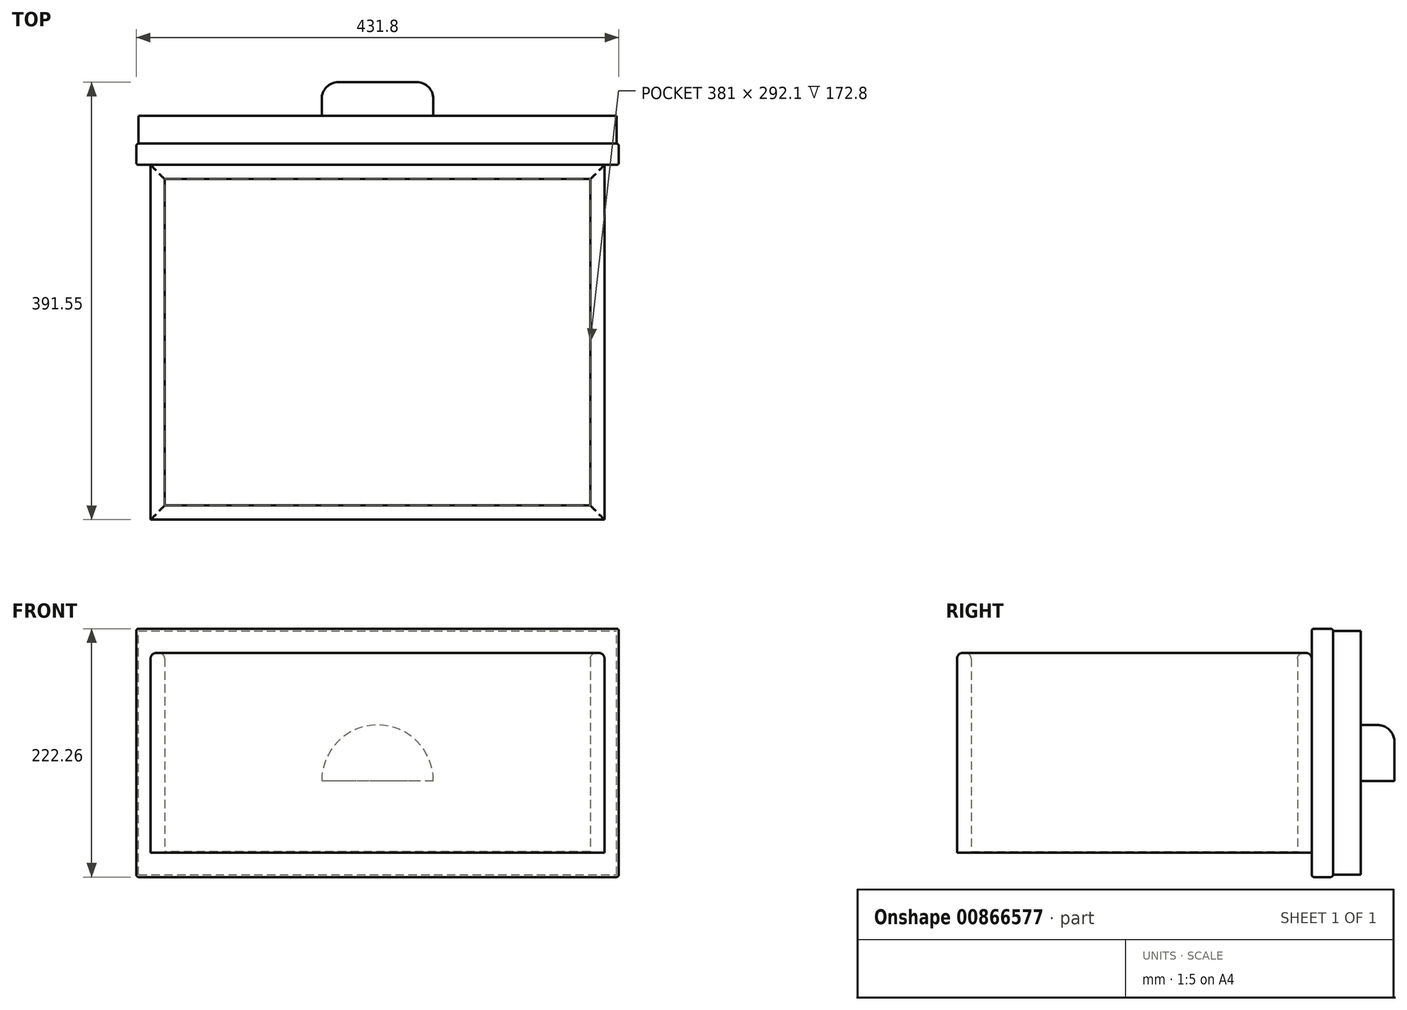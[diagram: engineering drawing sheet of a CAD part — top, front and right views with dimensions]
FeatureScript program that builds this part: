
annotation { "Feature Type Name" : "Feature", "Feature Type Description" : "" }
export const myFeature = defineFeature(function(context is Context, id is Id, definition is map)
    precondition{}
    {
        {
            var Q0;
            Q0=qCreatedBy(makeId("Top.planeOp"),FACE);
            var sketch = newSketch(context, id + "F0", { "sketchPlane" : qUnion([Q0])});
            skLineSegment(sketch, "E0.bottom", {"start": v(203.2, -158.75) * mm, "end": v(-203.2, -158.75) * mm});
            skLineSegment(sketch, "E0.top", {"start": v(203.2, 158.75) * mm, "end": v(-203.2, 158.75) * mm});
            skLineSegment(sketch, "E0.left", {"start": v(203.2, -158.75) * mm, "end": v(203.2, 158.75) * mm});
            skLineSegment(sketch, "E0.right", {"start": v(-203.2, -158.75) * mm, "end": v(-203.2, 158.75) * mm});
            skPoint(sketch, "E0.middle", {"position": v(0, 0) * mm});
            skLineSegment(sketch, "E1.0", {"start": v(190.5, 146.05) * mm, "end": v(-190.5, 146.05) * mm});
            skLineSegment(sketch, "E1.1", {"start": v(190.5, -146.05) * mm, "end": v(190.5, 146.05) * mm});
            skLineSegment(sketch, "E1.2", {"start": v(190.5, -146.05) * mm, "end": v(-190.5, -146.05) * mm});
            skLineSegment(sketch, "E1.3", {"start": v(-190.5, -146.05) * mm, "end": v(-190.5, 146.05) * mm});
            skSolve(sketch);
        }
        {
            var Q0;
            Q0=makeQuery(id+"F0.imprint","IMPRINT",FACE,{"disambiguationData":[TD([[makeQuery(id+"F0.imprint","IMPRINT",EDGE,{"derivedFrom":sQuery(id+"F0.wireOp",EDGE,"E0.bottom")}),-1.0]])]});
            extrude(context, id + "F1", {"entities" : qUnion([Q0]), "depth" : 177.8 * mm, "offsetDistance" : 25 * mm});
        }
        {
            var Q0;
            Q0=makeQuery(id+"F1.opExtrude","CAP_FACE",FACE,{"disambiguationData":[OSD([sQuery(id+"F0.wireOp",EDGE,"E0.bottom"),sQuery(id+"F0.wireOp",EDGE,"E0.top"),sQuery(id+"F0.wireOp",EDGE,"E0.left"),sQuery(id+"F0.wireOp",EDGE,"E0.right"),sQuery(id+"F0.wireOp",EDGE,"E1.0"),sQuery(id+"F0.wireOp",EDGE,"E1.1"),sQuery(id+"F0.wireOp",EDGE,"E1.2"),sQuery(id+"F0.wireOp",EDGE,"E1.3")])],"isStart":true});
            var sketch = newSketch(context, id + "F2", { "sketchPlane" : qUnion([Q0])});
            skLineSegment(sketch, "E2.bottom", {"start": v(203.2, -158.75) * mm, "end": v(-203.2, -158.75) * mm});
            skLineSegment(sketch, "E2.top", {"start": v(203.2, 158.75) * mm, "end": v(-203.2, 158.75) * mm});
            skLineSegment(sketch, "E2.left", {"start": v(203.2, -158.75) * mm, "end": v(203.2, 158.75) * mm});
            skLineSegment(sketch, "E2.right", {"start": v(-203.2, -158.75) * mm, "end": v(-203.2, 158.75) * mm});
            skPoint(sketch, "E2.middle", {"position": v(0, 0) * mm});
            skSolve(sketch);
        }
        {
            var Q0;
            Q0 = qSketchRegion(id + "F2", true);
            extrude(context, id + "F3", {"entities" : qUnion([Q0]), "operationType" : NewBodyOperationType.ADD, "depth" : 1 * mm, "offsetDistance" : 25 * mm});
        }
        {
            var Q0;
            Q0=makeQuery(id+"F3.boolean.opBoolean","MERGE",FACE,{"derivedFrom":[makeQuery(id+"F1.opExtrude","SWEPT_FACE",FACE,{"disambiguationData":[OSD([sQuery(id+"F0.wireOp",EDGE,"E0.top")])]}),makeQuery(id+"F3.opExtrude","SWEPT_FACE",FACE,{"disambiguationData":[OSD([sQuery(id+"F2.wireOp",EDGE,"E2.bottom")])]})]});
            var sketch = newSketch(context, id + "F4", { "sketchPlane" : qUnion([Q0])});
            skLineSegment(sketch, "E3", {"start": v(0, 0) * mm, "end": v(0, 177.8) * mm, "construction": true});
            skLineSegment(sketch, "E4", {"start": v(-203.2, 88.4) * mm, "end": v(203.2, 88.4) * mm, "construction": true});
            skLineSegment(sketch, "E5.bottom", {"start": v(215.9, -22.73) * mm, "end": v(-215.9, -22.73) * mm});
            skLineSegment(sketch, "E5.top", {"start": v(215.9, 199.53) * mm, "end": v(-215.9, 199.52) * mm});
            skLineSegment(sketch, "E5.left", {"start": v(215.9, -22.73) * mm, "end": v(215.9, 199.53) * mm});
            skLineSegment(sketch, "E5.right", {"start": v(-215.9, -22.73) * mm, "end": v(-215.9, 199.52) * mm});
            skPoint(sketch, "E5.middle", {"position": v(0, 88.4) * mm});
            skSolve(sketch);
        }
        {
            var Q0;
            Q0 = qSketchRegion(id + "F4", true);
            extrude(context, id + "F5", {"entities" : qUnion([Q0]), "depth" : 19.05 * mm, "offsetDistance" : 25 * mm});
        }
        {
            var Q0;
            Q0=makeQuery(id+"F1.opExtrude","CAP_EDGE",EDGE,{"disambiguationData":[OSD([sQuery(id+"F0.wireOp",EDGE,"E0.left")])],"isStart":false});
            var Q1;
            Q1=makeQuery(id+"F1.opExtrude","CAP_EDGE",EDGE,{"disambiguationData":[OSD([sQuery(id+"F0.wireOp",EDGE,"E1.1")])],"isStart":false});
            var Q2;
            Q2=makeQuery(id+"F1.opExtrude","CAP_EDGE",EDGE,{"disambiguationData":[OSD([sQuery(id+"F0.wireOp",EDGE,"E1.2")])],"isStart":false});
            var Q3;
            Q3=makeQuery(id+"F1.opExtrude","CAP_EDGE",EDGE,{"disambiguationData":[OSD([sQuery(id+"F0.wireOp",EDGE,"E0.bottom")])],"isStart":false});
            var Q4;
            Q4=makeQuery(id+"F1.opExtrude","CAP_EDGE",EDGE,{"disambiguationData":[OSD([sQuery(id+"F0.wireOp",EDGE,"E1.3")])],"isStart":false});
            var Q5;
            Q5=makeQuery(id+"F1.opExtrude","CAP_EDGE",EDGE,{"disambiguationData":[OSD([sQuery(id+"F0.wireOp",EDGE,"E0.right")])],"isStart":false});
            var Q6;
            Q6=makeQuery(id+"F1.opExtrude","CAP_FACE",FACE,{"disambiguationData":[OSD([sQuery(id+"F0.wireOp",EDGE,"E0.bottom"),sQuery(id+"F0.wireOp",EDGE,"E0.top"),sQuery(id+"F0.wireOp",EDGE,"E0.left"),sQuery(id+"F0.wireOp",EDGE,"E0.right"),sQuery(id+"F0.wireOp",EDGE,"E1.0"),sQuery(id+"F0.wireOp",EDGE,"E1.1"),sQuery(id+"F0.wireOp",EDGE,"E1.2"),sQuery(id+"F0.wireOp",EDGE,"E1.3")])],"isStart":false});
            fillet(context, id + "F6", {"entities" : qUnion([Q0, Q1, Q2, Q3, Q4, Q5, Q6]), "radius" : 5 * mm, "tangentPropagation" : true, "allowEdgeOverflow" : false});
        }
        {
            var Q0;
            Q0=makeQuery(id+"F5.opExtrude","CAP_FACE",FACE,{"disambiguationData":[OSD([sQuery(id+"F4.wireOp",EDGE,"E5.bottom"),sQuery(id+"F4.wireOp",EDGE,"E5.top"),sQuery(id+"F4.wireOp",EDGE,"E5.left"),sQuery(id+"F4.wireOp",EDGE,"E5.right")])],"isStart":false});
            var Q1;
            Q1=makeQuery(id+"F5.opExtrude","SWEPT_FACE",FACE,{"disambiguationData":[OSD([sQuery(id+"F4.wireOp",EDGE,"E5.top")])]});
            var Q2;
            Q2=makeQuery(id+"F5.opExtrude","SWEPT_FACE",FACE,{"disambiguationData":[OSD([sQuery(id+"F4.wireOp",EDGE,"E5.left")])]});
            var Q3;
            Q3=makeQuery(id+"F5.opExtrude","SWEPT_FACE",FACE,{"disambiguationData":[OSD([sQuery(id+"F4.wireOp",EDGE,"E5.bottom")])]});
            var Q4;
            Q4=makeQuery(id+"F5.opExtrude","SWEPT_FACE",FACE,{"disambiguationData":[OSD([sQuery(id+"F4.wireOp",EDGE,"E5.right")])]});
            fillet(context, id + "F7", {"entities" : qUnion([Q0, Q1, Q2, Q3, Q4]), "radius" : 2 * mm, "tangentPropagation" : true, "allowEdgeOverflow" : false});
        }
        {
            var Q0;
            Q0=makeQuery(id+"F5.opExtrude","CAP_FACE",FACE,{"disambiguationData":[OSD([sQuery(id+"F4.wireOp",EDGE,"E5.bottom"),sQuery(id+"F4.wireOp",EDGE,"E5.top"),sQuery(id+"F4.wireOp",EDGE,"E5.left"),sQuery(id+"F4.wireOp",EDGE,"E5.right")])],"isStart":false});
            extrude(context, id + "F8", {"entities" : qUnion([Q0]), "operationType" : NewBodyOperationType.ADD, "depth" : 25 * mm, "offsetDistance" : 25 * mm});
        }
        {
            var Q0;
            Q0=makeQuery(id+"F8.opExtrude","CAP_FACE",FACE,{"disambiguationData":[OSD([sQuery(id+"F4.wireOp",EDGE,"E5.bottom"),sQuery(id+"F4.wireOp",EDGE,"E5.top"),sQuery(id+"F4.wireOp",EDGE,"E5.left"),sQuery(id+"F4.wireOp",EDGE,"E5.right")])],"isStart":false});
            var sketch = newSketch(context, id + "F9", { "sketchPlane" : qUnion([Q0])});
            skArc(sketch, "E6", {"start": v(50, 63.3) * mm, "mid": v(0, 113.3) * mm, "end": v(-50, 63.3) * mm});
            skLineSegment(sketch, "E7", {"start": v(-50, 63.3) * mm, "end": v(50, 63.3) * mm});
            skSolve(sketch);
        }
        {
            var Q0;
            Q0 = qSketchRegion(id + "F9", true);
            extrude(context, id + "F10", {"entities" : qUnion([Q0]), "depth" : 30 * mm, "offsetDistance" : 25 * mm});
        }
        {
            var Q0;
            Q0=makeQuery(id+"F10.opExtrude","CAP_EDGE",EDGE,{"disambiguationData":[OSD([sQuery(id+"F9.wireOp",EDGE,"E6")])],"isStart":false});
            fillet(context, id + "F11", {"entities" : qUnion([Q0]), "radius" : 15 * mm, "tangentPropagation" : true, "allowEdgeOverflow" : false});
        }
    });
